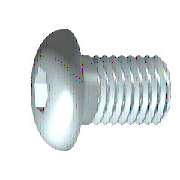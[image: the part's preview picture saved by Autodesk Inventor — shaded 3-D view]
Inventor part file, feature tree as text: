
AUTODESK INVENTOR PART (.ipt)
format: ipt  version: 2013 (Build 170138000, 138)  size: 195,072 bytes
history: native  units: mm (DEFAULTED — no unit token found)
features: sketch x2, extrude x1, plane x1, fillet x1
ambient origin geometry x7: Origin, YZ Plane, XY Plane, X Axis, Y Axis, Z Axis, Center Point
bodies: Solid1 (feature_tree), Body (feature_tree)
feature tree (5):
  extrude  "Slot"  Depth=1.59014mm
  plane  "Work Plane1"
  fillet  "Fillet2"  Radius=1.8542mm
  sketch  "Sketch1"  dims[d1=4.75976mm d2=1.59014mm d3=1.8542mm]
  sketch  "Sketch2"  dims[d4=1.1176mm d5=60.0deg d6=3.5052mm d7=3.5052mm d8=2.287693mm d9=6.6548mm d10=90.0deg d11=10.0mm d12=0.0mm d13=4.75976mm d14=0.0mm d15=0.486918mm d16=0.486918mm d17=1.6002mm d19=0.0mm d26=6.35mm d27=45.0deg d28=0.0mm d29=0.0mm d30=0.1mm]
